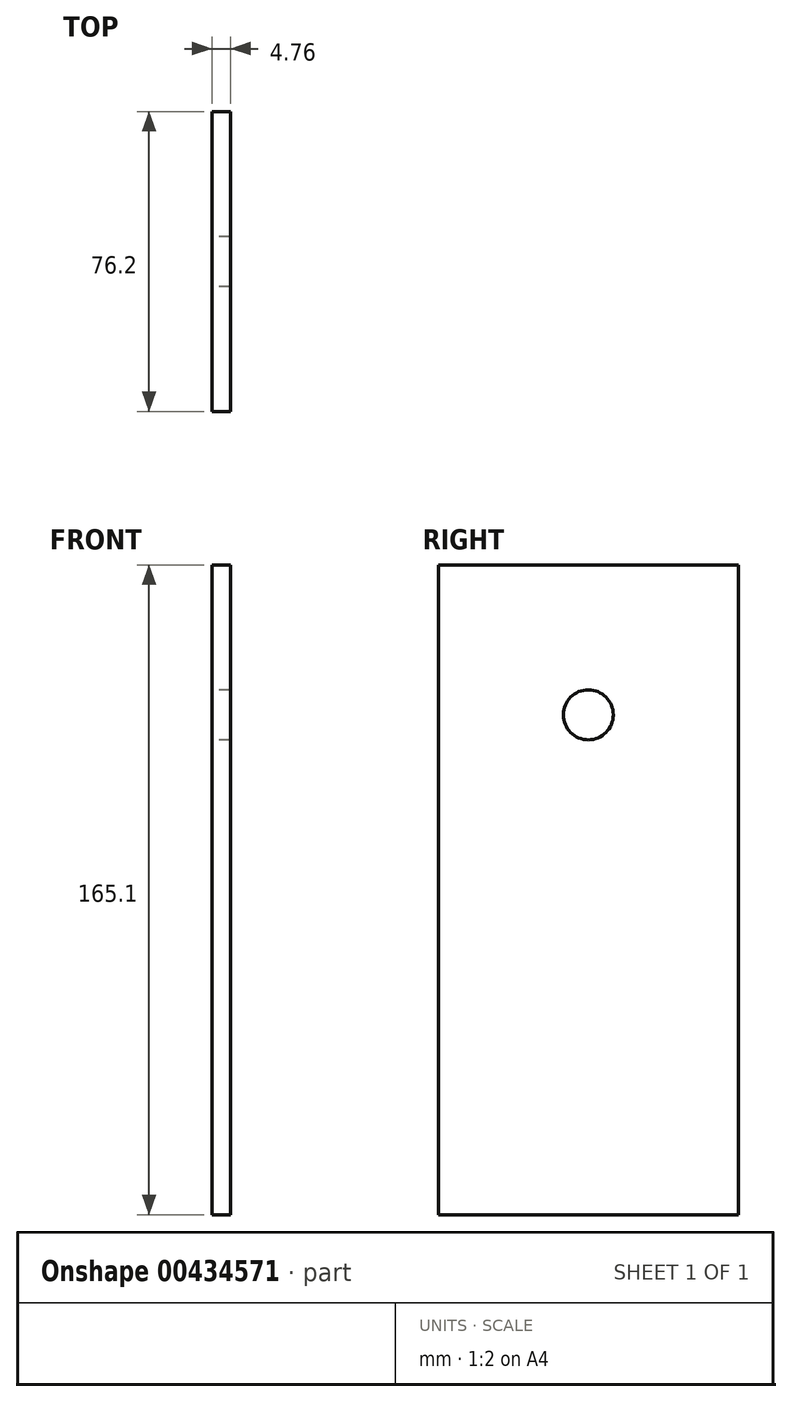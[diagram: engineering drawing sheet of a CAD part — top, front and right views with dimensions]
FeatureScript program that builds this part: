
annotation { "Feature Type Name" : "Feature", "Feature Type Description" : "" }
export const myFeature = defineFeature(function(context is Context, id is Id, definition is map)
    precondition{}
    {
        {
            var Q0;
            Q0=qCreatedBy(makeId("Right.planeOp"),FACE);
            var sketch = newSketch(context, id + "F0", { "sketchPlane" : qUnion([Q0])});
            skLineSegment(sketch, "E0.bottom", {"start": v(-53.45, 143.7) * mm, "end": v(22.75, 143.7) * mm});
            skLineSegment(sketch, "E0.top", {"start": v(-53.45, -21.4) * mm, "end": v(22.75, -21.4) * mm});
            skLineSegment(sketch, "E0.left", {"start": v(-53.45, 143.7) * mm, "end": v(-53.45, -21.4) * mm});
            skLineSegment(sketch, "E0.right", {"start": v(22.75, 143.7) * mm, "end": v(22.75, -21.4) * mm});
            skCircle(sketch, "E1", {"center": v(-15.35, 105.6) * mm, "radius": 6.35 * mm});
            skSolve(sketch);
        }
        {
            var Q0;
            Q0=makeQuery(id+"F0.imprint","IMPRINT",FACE,{"disambiguationData":[TD([[makeQuery(id+"F0.imprint","IMPRINT",EDGE,{"derivedFrom":sQuery(id+"F0.wireOp",EDGE,"E0.bottom")}),-1.0]])]});
            extrude(context, id + "F1", {"entities" : qUnion([Q0]), "depth" : 4.76 * mm});
        }
    });
